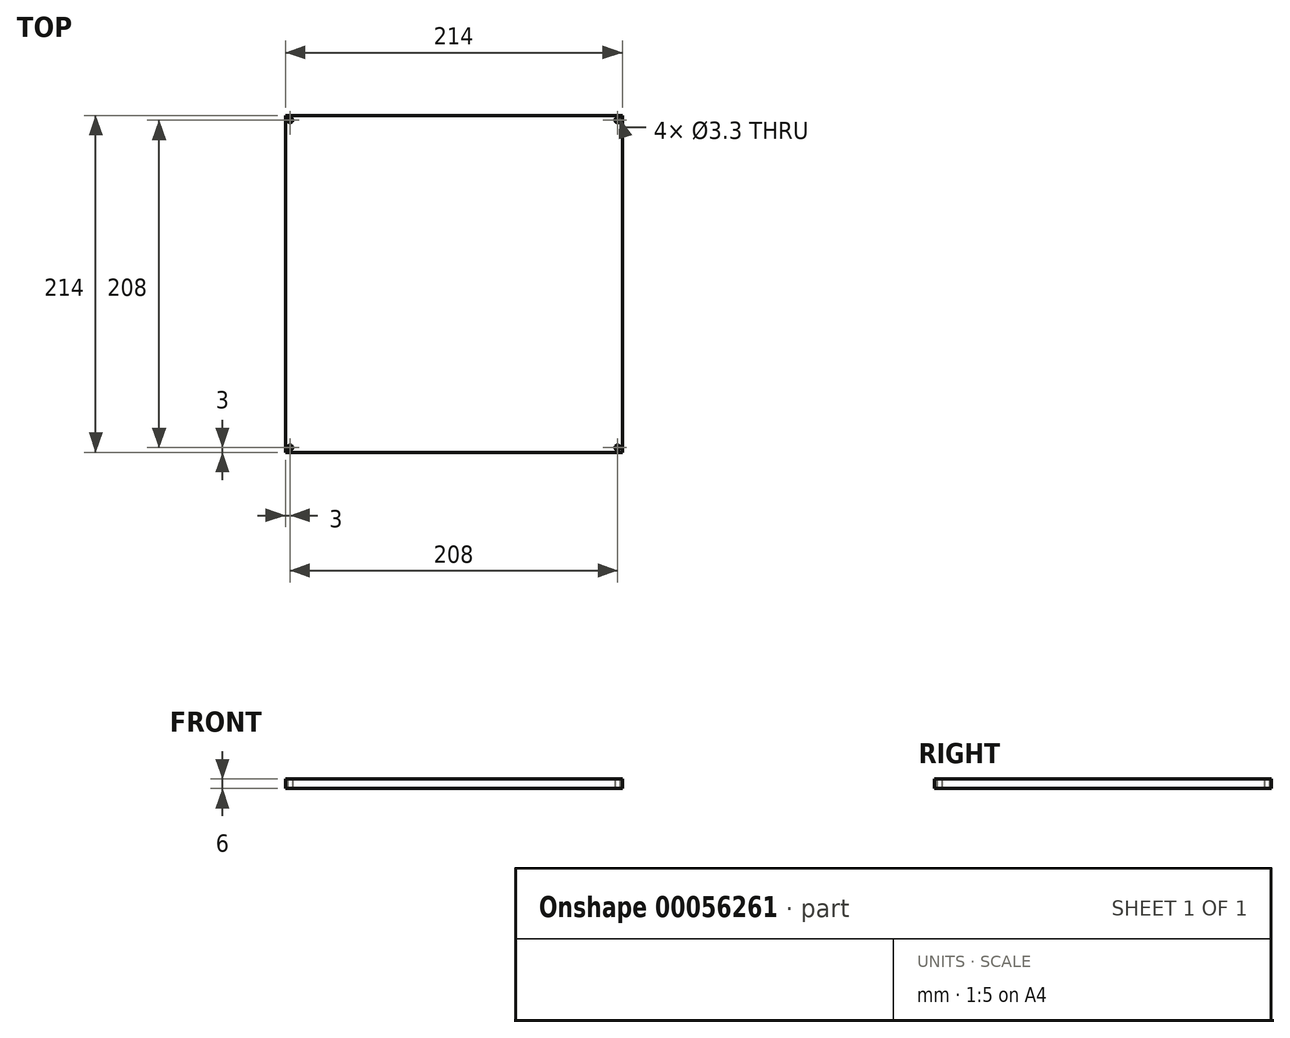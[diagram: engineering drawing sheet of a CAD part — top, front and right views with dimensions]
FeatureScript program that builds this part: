
annotation { "Feature Type Name" : "Feature", "Feature Type Description" : "" }
export const myFeature = defineFeature(function(context is Context, id is Id, definition is map)
    precondition{}
    {
        {
            var Q0;
            Q0=qCreatedBy(makeId("Top.planeOp"),FACE);
            var sketch = newSketch(context, id + "F0", { "sketchPlane" : qUnion([Q0])});
            skLineSegment(sketch, "E0.bottom", {"start": v(0, 0) * mm, "end": v(214, 0) * mm});
            skLineSegment(sketch, "E0.top", {"start": v(0, 214) * mm, "end": v(214, 214) * mm});
            skLineSegment(sketch, "E0.left", {"start": v(0, 0) * mm, "end": v(0, 214) * mm});
            skLineSegment(sketch, "E0.right", {"start": v(214, 0) * mm, "end": v(214, 214) * mm});
            skCircle(sketch, "E1", {"center": v(3, 211) * mm, "radius": 1.65 * mm});
            skCircle(sketch, "E2", {"center": v(211, 211) * mm, "radius": 1.65 * mm});
            skCircle(sketch, "E3", {"center": v(211, 3) * mm, "radius": 1.65 * mm});
            skCircle(sketch, "E4", {"center": v(3, 3) * mm, "radius": 1.65 * mm});
            skLineSegment(sketch, "E5", {"start": v(3, 211) * mm, "end": v(3, 214) * mm, "construction": true});
            skLineSegment(sketch, "E6", {"start": v(3, 211) * mm, "end": v(0, 211) * mm, "construction": true});
            skLineSegment(sketch, "E7", {"start": v(211, 211) * mm, "end": v(211, 214) * mm, "construction": true});
            skLineSegment(sketch, "E8", {"start": v(211, 211) * mm, "end": v(214, 211) * mm, "construction": true});
            skLineSegment(sketch, "E9", {"start": v(211, 3) * mm, "end": v(214, 3) * mm, "construction": true});
            skLineSegment(sketch, "E10", {"start": v(211, 3) * mm, "end": v(211, 0) * mm, "construction": true});
            skLineSegment(sketch, "E11", {"start": v(3, 3) * mm, "end": v(0, 3) * mm, "construction": true});
            skLineSegment(sketch, "E12", {"start": v(3, 3) * mm, "end": v(3, 0) * mm, "construction": true});
            skSolve(sketch);
        }
        {
            var Q0;
            Q0=qSketchRegion(id+"F0",true);
            extrude(context, id + "F1", {"entities" : qUnion([Q0]), "depth" : 6 * mm});
        }
    });
